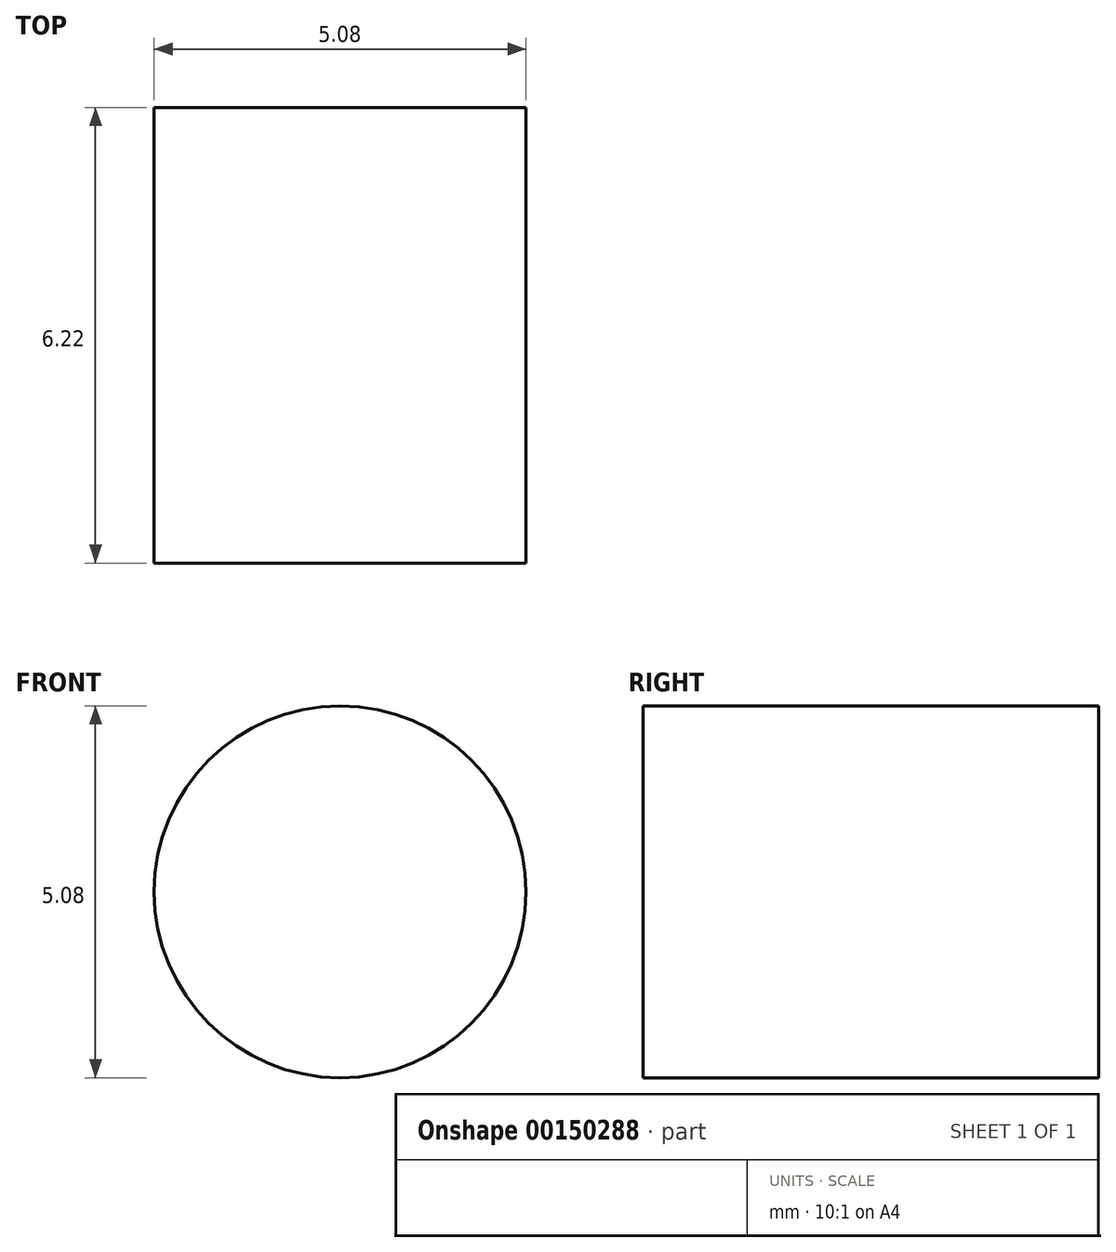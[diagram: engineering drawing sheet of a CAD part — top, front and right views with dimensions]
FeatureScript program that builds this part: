
annotation { "Feature Type Name" : "Feature", "Feature Type Description" : "" }
export const myFeature = defineFeature(function(context is Context, id is Id, definition is map)
    precondition{}
    {
        {
            var Q0;
            Q0=qCreatedBy(makeId("Front.planeOp"),FACE);
            var sketch = newSketch(context, id + "F0", { "sketchPlane" : qUnion([Q0])});
            skCircle(sketch, "E0", {"center": v(0, 0) * mm, "radius": 2.54 * mm});
            skSolve(sketch);
        }
        {
            var Q0;
            Q0 = qSketchRegion(id + "F0", true);
            extrude(context, id + "F1", {"entities" : qUnion([Q0]), "depth" : 6.22 * mm});
        }
    });
